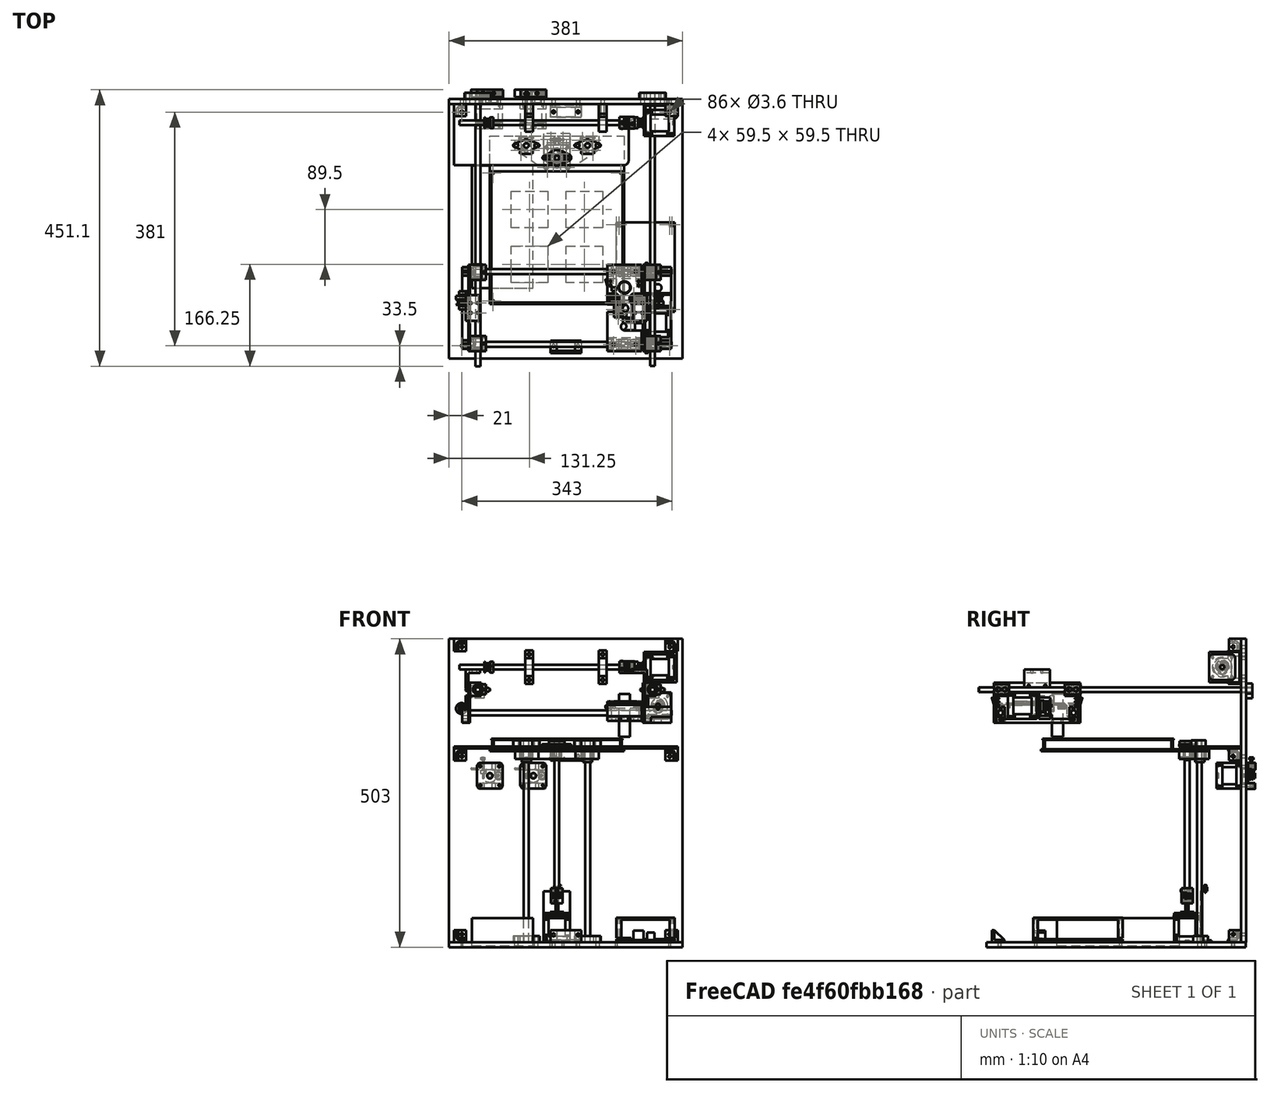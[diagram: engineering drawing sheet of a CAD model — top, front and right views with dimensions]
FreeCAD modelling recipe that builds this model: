
FCSTD DOCUMENT  (FreeCAD 0.16R6706 (Git))
Label: Montagem Plate superiores
License: All rights reserved
LicenseURL: http://en.wikipedia.org/wiki/All_rights_reserved
objects: Part::FeaturePython×11, Part::Cylinder×7, Part::Compound×1, Part::Box×1
note: 20 computed .brp shape members not serialized (recipe doc carries the construction recipe); baked Part::Feature solids carry a one-line shape summary decoded from their .brp

FEATURE [Part::FeaturePython] Montagem_Plate_Extrusora_01  # a2plus imported part (geometry in sourceFile) (typed FeaturePython)
  Placement = pos=(112,0,57) rot=(0,0,1;0rad)
  fixedPosition = true
  sourceFile = <path> Plate Extrusora.FCStd
  timeLastImport = 1.50665e+09
  updateColors = true
FEATURE [Part::Cylinder] Cylinder
  Angle = 360
  Height = 342
  Placement = pos=(-153,130,44.3) rot=(0,1,0;1.5708rad)
  Radius = 4
FEATURE [Part::Cylinder] Cylinder001
  Angle = 360
  Height = 342
  Placement = pos=(-153,11,44.3) rot=(0,1,0;1.5708rad)
  Radius = 4
FEATURE [Part::FeaturePython] Montagem_Plate_Y_Direita_01  # a2plus imported part (geometry in sourceFile) (typed FeaturePython)
  Placement = pos=(-140,0,28.3) rot=(0.57735,-0.57735,-0.57735;2.0944rad)
  fixedPosition = false
  sourceFile = <path> Plate Y Direita.FCStd
  timeLastImport = 1.50829e+09
  updateColors = true
FEATURE [Part::FeaturePython] Montagem_Plate_Y_Esquerda_01  # a2plus imported part (geometry in sourceFile) (typed FeaturePython)
  Placement = pos=(142,141,28.3) rot=(0.57735,0.57735,0.57735;2.0944rad)
  fixedPosition = false
  sourceFile = <path> Plate Y Esquerda.FCStd
  timeLastImport = 1.50829e+09
  updateColors = true
FEATURE [Part::Compound] Compound  label="Grupo X"
  Links = -> [Montagem_Plate_Y_Esquerda_01,Montagem_Plate_Y_Direita_01,Cylinder001,Cylinder,Montagem_Plate_Extrusora_01]
  Placement = pos=(0,-219.5,0.7) rot=(0,0,1;0rad)
FEATURE [Part::Cylinder] Cylinder002
  Angle = 360
  Height = 446
  Placement = pos=(-127.3,202,82.6) rot=(1,0,0;1.5708rad)
  Radius = 4
FEATURE [Part::Cylinder] Cylinder003
  Angle = 360
  Height = 446
  Placement = pos=(157.7,202.5,82.6315) rot=(0.57735,0.57735,-0.57735;2.0944rad)
  Radius = 4
FEATURE [Part::FeaturePython] Montagem_Frente_01  # a2plus imported part (geometry in sourceFile) (typed FeaturePython)
  Placement = pos=(-174.3,-231.5,-329.368) rot=(0,0.707107,0.707107;3.14159rad)
  fixedPosition = false
  sourceFile = <path> Frente.FCStd
  timeLastImport = 1.50829e+09
  updateColors = true
FEATURE [Part::FeaturePython] Montagem_Fundo_01  # a2plus imported part (geometry in sourceFile) (typed FeaturePython)
  Placement = pos=(206.7,192,-329.4) rot=(1,0,0;1.5708rad)
  fixedPosition = false
  sourceFile = <path> Fundo.FCStd
  timeLastImport = 1.50829e+09
  updateColors = true
FEATURE [Part::FeaturePython] Montagem_Mesa_01  label="Mesa"  # a2plus imported part (geometry in sourceFile) (typed FeaturePython)
  Placement = pos=(1.70001,-33,1) rot=(0,0,1;3.14159rad)
  fixedPosition = false
  sourceFile = <path> Mesa.FCStd
  timeLastImport = 1.50675e+09
  updateColors = true
FEATURE [Part::Cylinder] Cylinder004
  Angle = 360
  Height = 329
  Placement = pos=(-48.3,115.8,-329.4) rot=(0,0,1;3.14159rad)
  Radius = 4
FEATURE [Part::Cylinder] Cylinder005
  Angle = 360
  Height = 329
  Placement = pos=(51.7,115.8,-329.4) rot=(0,0,1;3.14159rad)
  Radius = 4
FEATURE [Part::Cylinder] Cylinder006
  Angle = 360
  Height = 257
  Placement = pos=(1.4294,95.8,-257.9) rot=(0,0,1;3.14159rad)
  Radius = 4
FEATURE [Part::Box] Box  label="Cube"
  Height = 45
  Length = 100
  Placement = pos=(-137.042,-116.318,-335) rot=(0,0,1;0rad)
  Width = 200
FEATURE [Part::FeaturePython] Teto_01  # a2plus imported part (geometry in sourceFile) (typed FeaturePython)
  Placement = pos=(206.7,-231,165.6) rot=(0,0,1;0rad)
  fixedPosition = false
  sourceFile = <path>
  timeLastImport = 1.50665e+09
  updateColors = true
FEATURE [Part::FeaturePython] Lado_Direito_01  # a2plus imported part (geometry in sourceFile) (typed FeaturePython)
  Placement = pos=(-174.3,-19.5,-81.9) rot=(0.57735,0.57735,0.57735;2.0944rad)
  fixedPosition = false
  sourceFile = <path> Direito.FCStd
  timeLastImport = 1.50665e+09
  updateColors = true
FEATURE [Part::FeaturePython] Lado_Esquerdo_01  # a2plus imported part (geometry in sourceFile) (typed FeaturePython)
  Placement = pos=(198.7,-20,-81.8685) rot=(0.57735,0.57735,0.57735;2.0944rad)
  fixedPosition = false
  sourceFile = <path> Esquerdo.FCStd
  timeLastImport = 1.50665e+09
  updateColors = true
FEATURE [Part::FeaturePython] Montagem_Mezanino_01  # a2plus imported part (geometry in sourceFile) (typed FeaturePython)
  Placement = pos=(16.2,184,-10) rot=(1,0,0;3.14159rad)
  fixedPosition = false
  sourceFile = <path> Mezanino.FCStd
  timeLastImport = 1.50829e+09
  updateColors = true
FEATURE [Part::FeaturePython] Montagem_Piso_01  # a2plus imported part (geometry in sourceFile) (typed FeaturePython)
  Placement = pos=(206.7,-231.5,-337.4) rot=(0,0,1;0rad)
  fixedPosition = false
  sourceFile = <path> Piso.FCStd
  timeLastImport = 1.50712e+09
  updateColors = true
note: 11 file-system paths scrubbed to <path> (originals preserved in the JSON sidecar)
